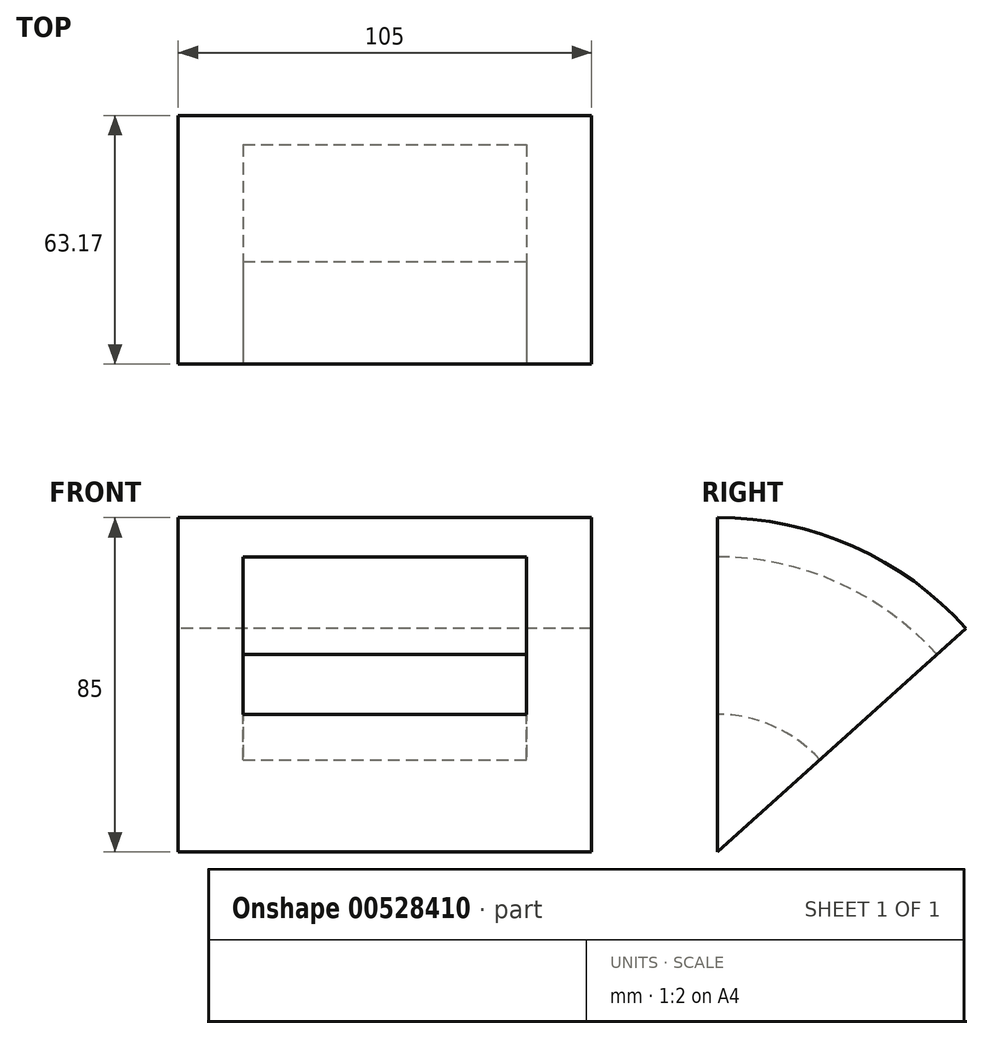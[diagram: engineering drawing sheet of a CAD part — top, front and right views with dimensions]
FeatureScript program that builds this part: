
annotation { "Feature Type Name" : "Feature", "Feature Type Description" : "" }
export const myFeature = defineFeature(function(context is Context, id is Id, definition is map)
    precondition{}
    {
        {
            var Q0;
            Q0=qCreatedBy(makeId("Front.planeOp"),FACE);
            var sketch = newSketch(context, id + "F0", { "sketchPlane" : qUnion([Q0])});
            skLineSegment(sketch, "E0.bottom", {"start": v(52.5, 42.5) * mm, "end": v(-52.5, 42.5) * mm});
            skLineSegment(sketch, "E0.top", {"start": v(52.5, -42.5) * mm, "end": v(-52.5, -42.5) * mm});
            skLineSegment(sketch, "E0.left", {"start": v(52.5, 42.5) * mm, "end": v(52.5, -42.5) * mm});
            skLineSegment(sketch, "E0.right", {"start": v(-52.5, 42.5) * mm, "end": v(-52.5, -42.5) * mm});
            skPoint(sketch, "E0.middle", {"position": v(0, 0) * mm});
            skLineSegment(sketch, "E1.bottom", {"start": v(-36, 32.5) * mm, "end": v(36, 32.5) * mm});
            skLineSegment(sketch, "E1.top", {"start": v(-36, -7.5) * mm, "end": v(36, -7.5) * mm});
            skLineSegment(sketch, "E1.left", {"start": v(-36, 32.5) * mm, "end": v(-36, -7.5) * mm});
            skLineSegment(sketch, "E1.right", {"start": v(36, 32.5) * mm, "end": v(36, -7.5) * mm});
            skSolve(sketch);
        }
        {
            var Q0;
            Q0=makeQuery(id+"F0.imprint","IMPRINT",FACE,{"disambiguationData":[TD([[makeQuery(id+"F0.imprint","IMPRINT",EDGE,{"derivedFrom":sQuery(id+"F0.wireOp",EDGE,"E0.bottom")}),1.0]])]});
            var Q1;
            Q1=sQuery(id+"F0.wireOp",EDGE,"E0.left");
            var Q2;
            Q2=sQuery(id+"F0.wireOp",EDGE,"E0.top");
            revolve(context, id + "F1", {"entities" : qUnion([Q0]), "surfaceEntities" : qUnion([Q1]), "axis" : qUnion([Q2]), "revolveType" : RevolveType.ONE_DIRECTION, "angle" : 48 * degree});
        }
        {
            var Q0;
            Q0=makeQuery(id+"F1.opRevolve","CAP_EDGE",EDGE,{"disambiguationData":[OSD([sQuery(id+"F0.wireOp",EDGE,"E0.bottom")])],"isStart":false});
            var Q1;
            Q1=sQuery(id+"F0.wireOp",EDGE,"E0.bottom");
            cPlane(context, id + "F2", {"entities" : qUnion([Q0, Q1]), "cplaneType" : CPlaneType.LINE_ANGLE, "offset" : 25 * mm, "angle" : 0 * degree, "width" : 150 * mm, "height" : 150 * mm});
        }
    });
